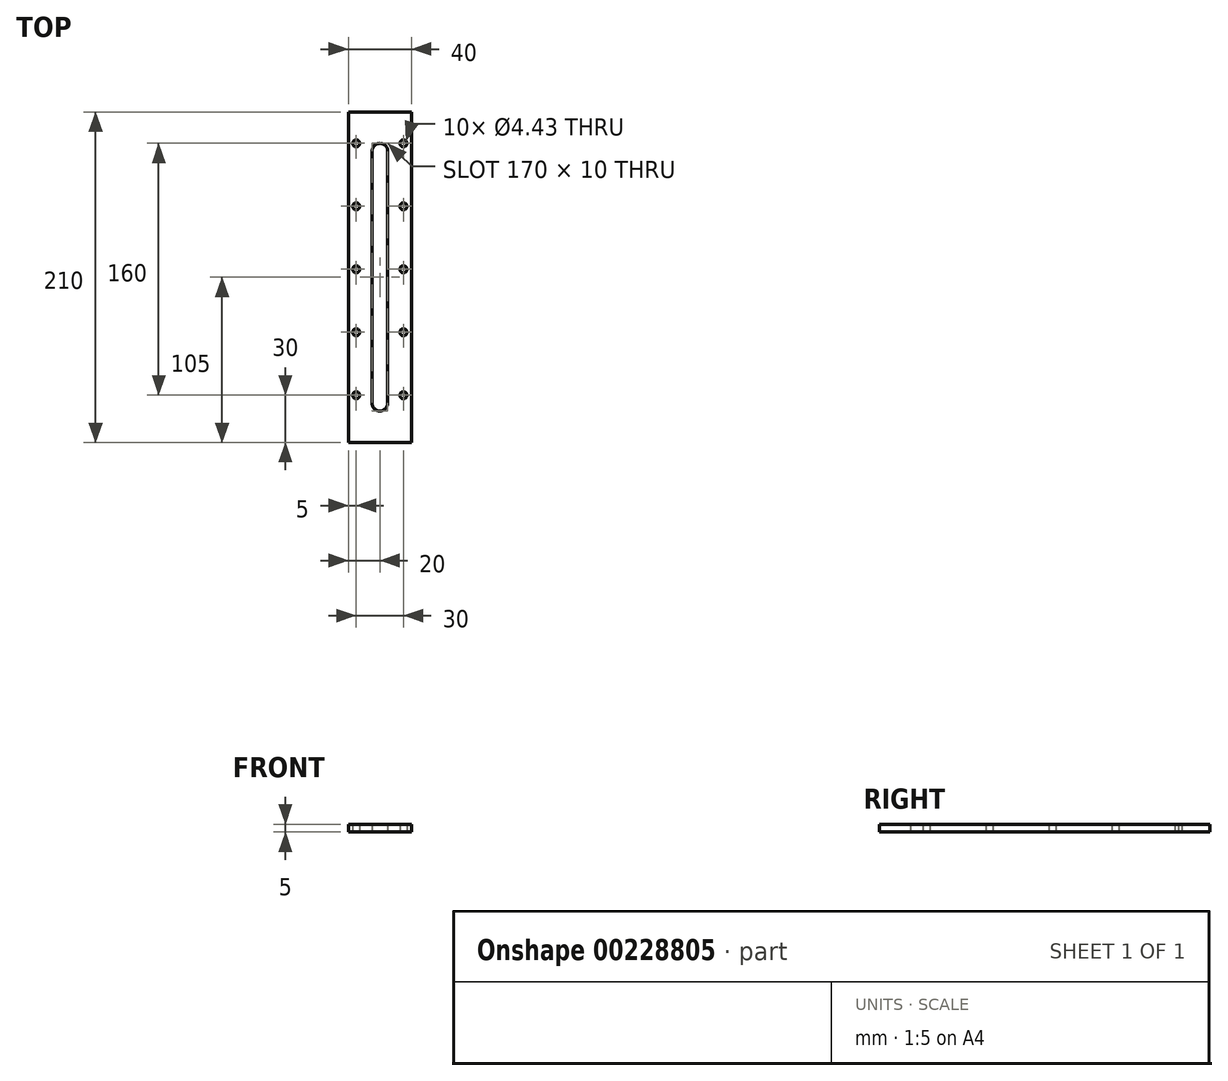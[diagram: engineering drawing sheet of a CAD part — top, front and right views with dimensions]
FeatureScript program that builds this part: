
annotation { "Feature Type Name" : "Feature", "Feature Type Description" : "" }
export const myFeature = defineFeature(function(context is Context, id is Id, definition is map)
    precondition{}
    {
        {
            var Q0;
            Q0=qCreatedBy(makeId("Top.planeOp"),FACE);
            var sketch = newSketch(context, id + "F0", { "sketchPlane" : qUnion([Q0])});
            skLineSegment(sketch, "E0.bottom", {"start": v(-20, 105) * mm, "end": v(20, 105) * mm});
            skLineSegment(sketch, "E0.top", {"start": v(-20, -105) * mm, "end": v(20, -105) * mm});
            skLineSegment(sketch, "E0.left", {"start": v(-20, 105) * mm, "end": v(-20, -105) * mm});
            skLineSegment(sketch, "E0.right", {"start": v(20, 105) * mm, "end": v(20, -105) * mm});
            skLineSegment(sketch, "E1.bottom", {"start": v(-5, 85) * mm, "end": v(5, 85) * mm});
            skLineSegment(sketch, "E1.top", {"start": v(-5, -85) * mm, "end": v(5, -85) * mm});
            skLineSegment(sketch, "E1.left", {"start": v(-5, 85) * mm, "end": v(-5, -85) * mm});
            skLineSegment(sketch, "E1.right", {"start": v(5, 85) * mm, "end": v(5, -85) * mm});
            skCircle(sketch, "E2", {"center": v(-15, -75) * mm, "radius": 2.22 * mm});
            skCircle(sketch, "E3", {"center": v(15, -75) * mm, "radius": 2.22 * mm});
            skCircle(sketch, "E4.0.1.0", {"center": v(15, -35) * mm, "radius": 2.22 * mm});
            skCircle(sketch, "E4.0.1.1", {"center": v(-15, -35) * mm, "radius": 2.22 * mm});
            skCircle(sketch, "E4.0.2.0", {"center": v(15, 5) * mm, "radius": 2.22 * mm});
            skCircle(sketch, "E4.0.2.1", {"center": v(-15, 5) * mm, "radius": 2.22 * mm});
            skCircle(sketch, "E4.0.3.0", {"center": v(15, 45) * mm, "radius": 2.22 * mm});
            skCircle(sketch, "E4.0.3.1", {"center": v(-15, 45) * mm, "radius": 2.22 * mm});
            skCircle(sketch, "E4.0.4.0", {"center": v(15, 85) * mm, "radius": 2.22 * mm});
            skCircle(sketch, "E4.0.4.1", {"center": v(-15, 85) * mm, "radius": 2.22 * mm});
            skLineSegment(sketch, "E4.direction1", {"start": v(-15, -75) * mm, "end": v(47, -78.1) * mm, "construction": true});
            skLineSegment(sketch, "E4.direction2", {"start": v(-15, -75) * mm, "end": v(-15, -35) * mm, "construction": true});
            skSolve(sketch);
        }
        {
            var Q0;
            Q0=makeQuery(id+"F0.imprint","IMPRINT",FACE,{"disambiguationData":[TD([[makeQuery(id+"F0.imprint","IMPRINT",EDGE,{"derivedFrom":sQuery(id+"F0.wireOp",EDGE,"E0.bottom")}),-1.0]])]});
            extrude(context, id + "F1", {"entities" : qUnion([Q0]), "depth" : 2.5 * mm, "hasSecondDirection" : true, "secondDirectionOppositeDirection" : true, "secondDirectionDepth" : 2.5 * mm});
        }
        {
            var Q0;
            Q0=makeQuery(id+"F1.opExtrude","SWEPT_EDGE",EDGE,{"disambiguationData":[OSD([sQuery(id+"F0.wireOp",EDGE,"E1.bottom"),sQuery(id+"F0.wireOp",EDGE,"E1.left")])]});
            var Q1;
            Q1=makeQuery(id+"F1.opExtrude","SWEPT_EDGE",EDGE,{"disambiguationData":[OSD([sQuery(id+"F0.wireOp",EDGE,"E1.bottom"),sQuery(id+"F0.wireOp",EDGE,"E1.right")])]});
            var Q2;
            Q2=makeQuery(id+"F1.opExtrude","SWEPT_EDGE",EDGE,{"disambiguationData":[OSD([sQuery(id+"F0.wireOp",EDGE,"E1.top"),sQuery(id+"F0.wireOp",EDGE,"E1.left")])]});
            var Q3;
            Q3=makeQuery(id+"F1.opExtrude","SWEPT_EDGE",EDGE,{"disambiguationData":[OSD([sQuery(id+"F0.wireOp",EDGE,"E1.top"),sQuery(id+"F0.wireOp",EDGE,"E1.right")])]});
            fillet(context, id + "F2", {"entities" : qUnion([Q0, Q1, Q2, Q3]), "radius" : 5 * mm, "tangentPropagation" : true, "allowEdgeOverflow" : false});
        }
    });
